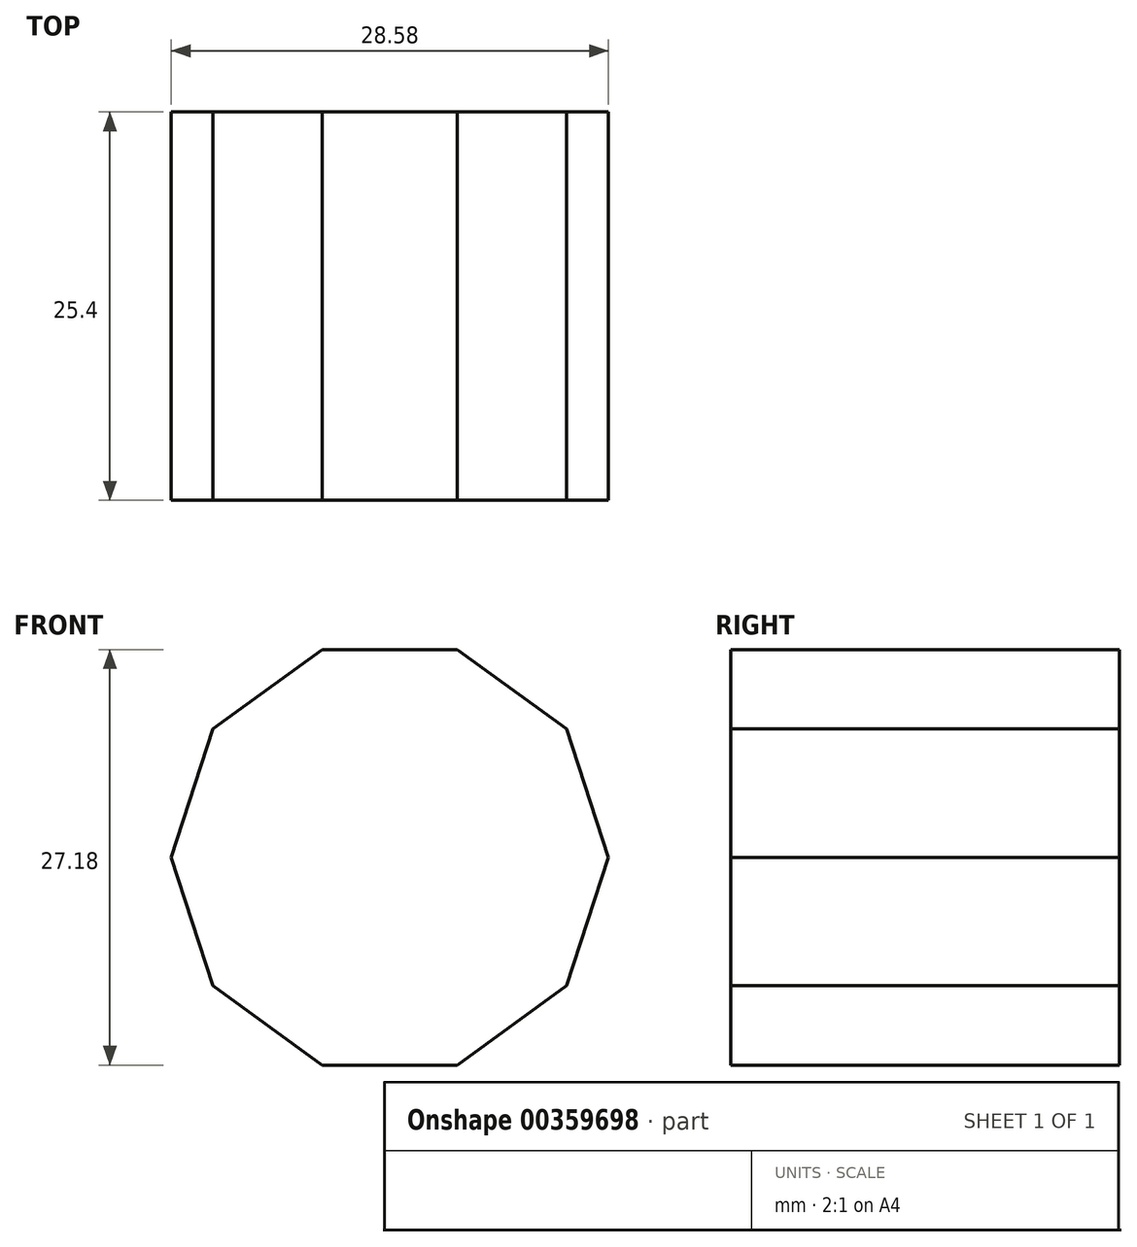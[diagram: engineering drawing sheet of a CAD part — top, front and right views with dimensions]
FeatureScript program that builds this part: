
annotation { "Feature Type Name" : "Feature", "Feature Type Description" : "" }
export const myFeature = defineFeature(function(context is Context, id is Id, definition is map)
    precondition{}
    {
        {
            var Q0;
            Q0=qCreatedBy(makeId("Front.planeOp"),FACE);
            var sketch = newSketch(context, id + "F0", { "sketchPlane" : qUnion([Q0])});
            skLineSegment(sketch, "E0", {"start": v(0, 0) * mm, "end": v(0, 13.59) * mm});
            skCircle(sketch, "E1.cCircle", {"center": v(0, 0) * mm, "radius": 13.59 * mm, "construction": true});
            skLineSegment(sketch, "E1.0", {"start": v(-4.42, 13.59) * mm, "end": v(4.42, 13.59) * mm});
            skLineSegment(sketch, "E1.1", {"start": v(4.42, 13.59) * mm, "end": v(11.56, 8.4) * mm});
            skLineSegment(sketch, "E1.2", {"start": v(11.56, 8.4) * mm, "end": v(14.29, 0) * mm});
            skLineSegment(sketch, "E1.3", {"start": v(14.29, 0) * mm, "end": v(11.56, -8.4) * mm});
            skLineSegment(sketch, "E1.4", {"start": v(11.56, -8.4) * mm, "end": v(4.42, -13.59) * mm});
            skLineSegment(sketch, "E1.5", {"start": v(4.42, -13.59) * mm, "end": v(-4.42, -13.59) * mm});
            skLineSegment(sketch, "E1.6", {"start": v(-4.42, -13.59) * mm, "end": v(-11.56, -8.4) * mm});
            skLineSegment(sketch, "E1.7", {"start": v(-11.56, -8.4) * mm, "end": v(-14.29, 0) * mm});
            skLineSegment(sketch, "E1.8", {"start": v(-14.29, 0) * mm, "end": v(-11.56, 8.4) * mm});
            skLineSegment(sketch, "E1.9", {"start": v(-11.56, 8.4) * mm, "end": v(-4.42, 13.59) * mm});
            skPoint(sketch, "E1.0.midPoint", {"position": v(0, 13.59) * mm});
            skSolve(sketch);
        }
        {
            var Q0;
            {var subQ3=sQuery(id+"F0.wireOp",EDGE,"E1.1");Q0=makeQuery(id+"F0.imprint","IMPRINT",FACE,{"disambiguationData":[TD([[makeQuery(id+"F0.imprint","IMPRINT",EDGE,{"derivedFrom":subQ3}),-1.0]])]});}
            extrude(context, id + "F1", {"entities" : qUnion([Q0]), "depth" : 25.4 * mm});
        }
    });
